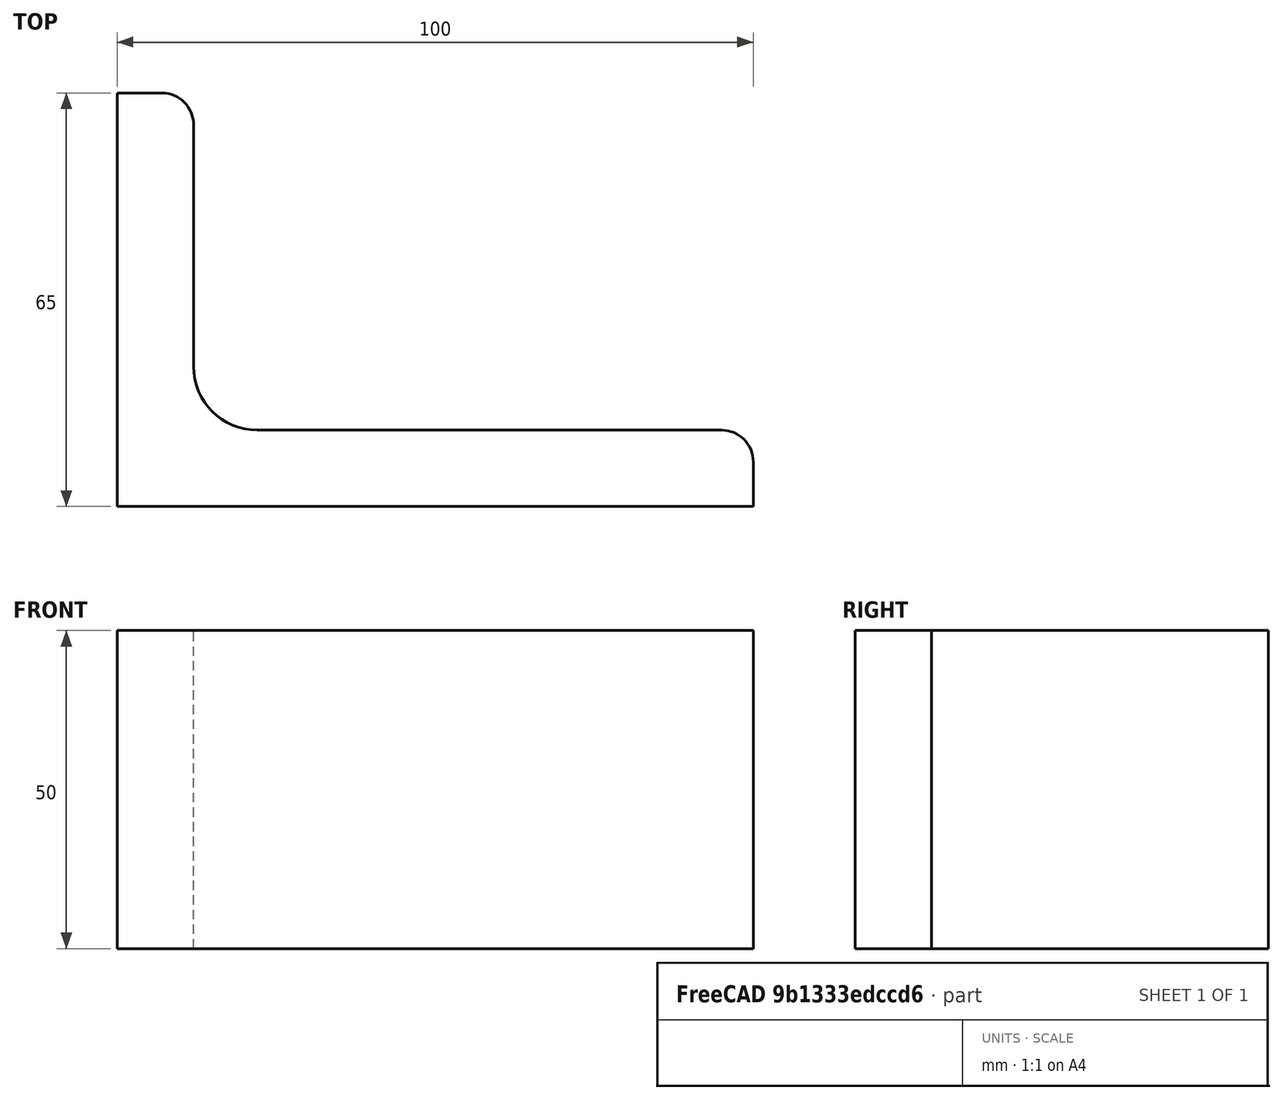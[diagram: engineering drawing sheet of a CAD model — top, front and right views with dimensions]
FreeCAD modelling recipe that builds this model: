
FCSTD DOCUMENT  (FreeCAD 0.15R4671 (Git))
Label: Angle Bar 100x65x12 EN10056 S235JR
License: All rights reserved
LicenseURL: http://en.wikipedia.org/wiki/All_rights_reserved
objects: Sketcher::SketchObject×1, Part::Extrusion×1
note: 2 computed .brp shape members not serialized (recipe doc carries the construction recipe); baked Part::Feature solids carry a one-line shape summary decoded from their .brp

FEATURE [Sketcher::SketchObject] Sketch
  sketch-geometry (9):
    g0: LineSegment StartX=0 StartY=0 StartZ=0 EndX=100 EndY=0 EndZ=0
    g1: LineSegment StartX=100 StartY=0 StartZ=0 EndX=100 EndY=7 EndZ=0
    g2: LineSegment StartX=95 StartY=12 StartZ=0 EndX=22 EndY=12 EndZ=0
    g3: LineSegment StartX=0 StartY=0 StartZ=0 EndX=0 EndY=65 EndZ=0
    g4: LineSegment StartX=0 StartY=65 StartZ=0 EndX=7 EndY=65 EndZ=0
    g5: LineSegment StartX=12 StartY=60 StartZ=0 EndX=12 EndY=22 EndZ=0
    g6: ArcOfCircle CenterX=22 CenterY=22 CenterZ=0 NormalX=0 NormalY=0 NormalZ=1 Radius=10 StartAngle=3.14159 EndAngle=4.71239
    g7: ArcOfCircle CenterX=7 CenterY=60 CenterZ=0 NormalX=0 NormalY=0 NormalZ=1 Radius=5 StartAngle=0 EndAngle=1.5708
    g8: ArcOfCircle CenterX=95 CenterY=7 CenterZ=0 NormalX=0 NormalY=0 NormalZ=1 Radius=5 StartAngle=0 EndAngle=1.5708
  constraints (23):
    c: Coincident(g0,g-1)
    c: Horizontal(g0)
    c: Coincident(g1,g0)
    c: Vertical(g1)
    c: Horizontal(g2)
    c: Coincident(g3,g-1)
    c: Vertical(g3)
    c: Coincident(g4,g3)
    c: Horizontal(g4)
    c: Vertical(g5)
    c: Tangent(g5,g6) = -1.5708
    c: Tangent(g2,g6) = 1.5708
    c: Tangent(g4,g7) = 1.5708
    c: Tangent(g5,g7) = 1.5708
    c: Tangent(g2,g8) = -1.5708
    c: Tangent(g1,g8) = -1.5708
    c: DistanceX(g0) = 100
    c: DistanceY(g3) = 65
    c: DistanceY(g0,g2) = 12
    c: DistanceX(g3,g5) = 12
    c: Radius(g6) = 10
    c: Radius(g8) = 5
    c: Radius(g7) = 5
FEATURE [Part::Extrusion] Extrude  label="Angle Bar 100x65x12 EN10056 S235JR"
  Base = -> Sketch
  Dir = (0,0,50)
  Solid = true
